# Revit family: Trapezblechhänger mit Bohrung
name_source: partatom
category: Allgemeines Modell
revit_build: Autodesk Revit 2018 (Build: 20190510_1515(x64)
units: mm (PartAtom-declared; Revit-internal decimal feet)

## family parameters
Arbeitsebenenbasiert = Ja
Beim Laden mit Abzugskörper schneiden = Nein
Bemaßung runder Anschluss = Durchmesser verwenden
Gemeinsam genutzt = Ja
Immer vertikal = Nein
Kann Basisbauteil für Bewehrung sein = Nein
Raumberechnungspunkt = Nein
Teiletyp = Normal

## types (1)
- Trapezblechhänger mit Bohrung 16,5 mm
    Anschlussgewinde = M10
    Artikelnummer = 0783801
    Ausführung = eingeschweißte Mutter
    Befestigungsloch = 9.5 mm
    Breite Aufnahme (innen) = 22.5 mm
    Breite Material = 25 mm
    EAN = 4250928418807
    Fabrikat = MEFA
    Firma = MEFA Befestigungs- und Montagesysteme GmbH
    Gewicht = 0.10 kg
    Gewicht pro Bauteil = 0.10 kg
    Höhe = 92.5 mm
    Kurztext1 = Trapezblechhänger mit Bohrung
    Kurztext2 = 16,5 mm
    Material = Stahl
    Materialname = S235/DD11
    Mengeneinheit = St
    Mutter DIN 928 = Mutter DIN 928 : Mutter DIN 928 M10
    Oberflaeche = galvanisch verzinkt
    Schalldämmeinlage = ohne Dämmung
    Stärke Material = 3 mm  [stored 0.00984252 ft]
    Trapezblechhänger = Trapezblechhänger : MEFA Trapezblechhänger Bohrung 16,5 mm
    Vorgabe-Ansicht = 1219 mm
    max. zul. Last = 2.00 kN
    vpe = 100

note: [stored X ft] marks values corroborated as IEEE doubles in the binary element streams (Revit-internal decimal feet)
